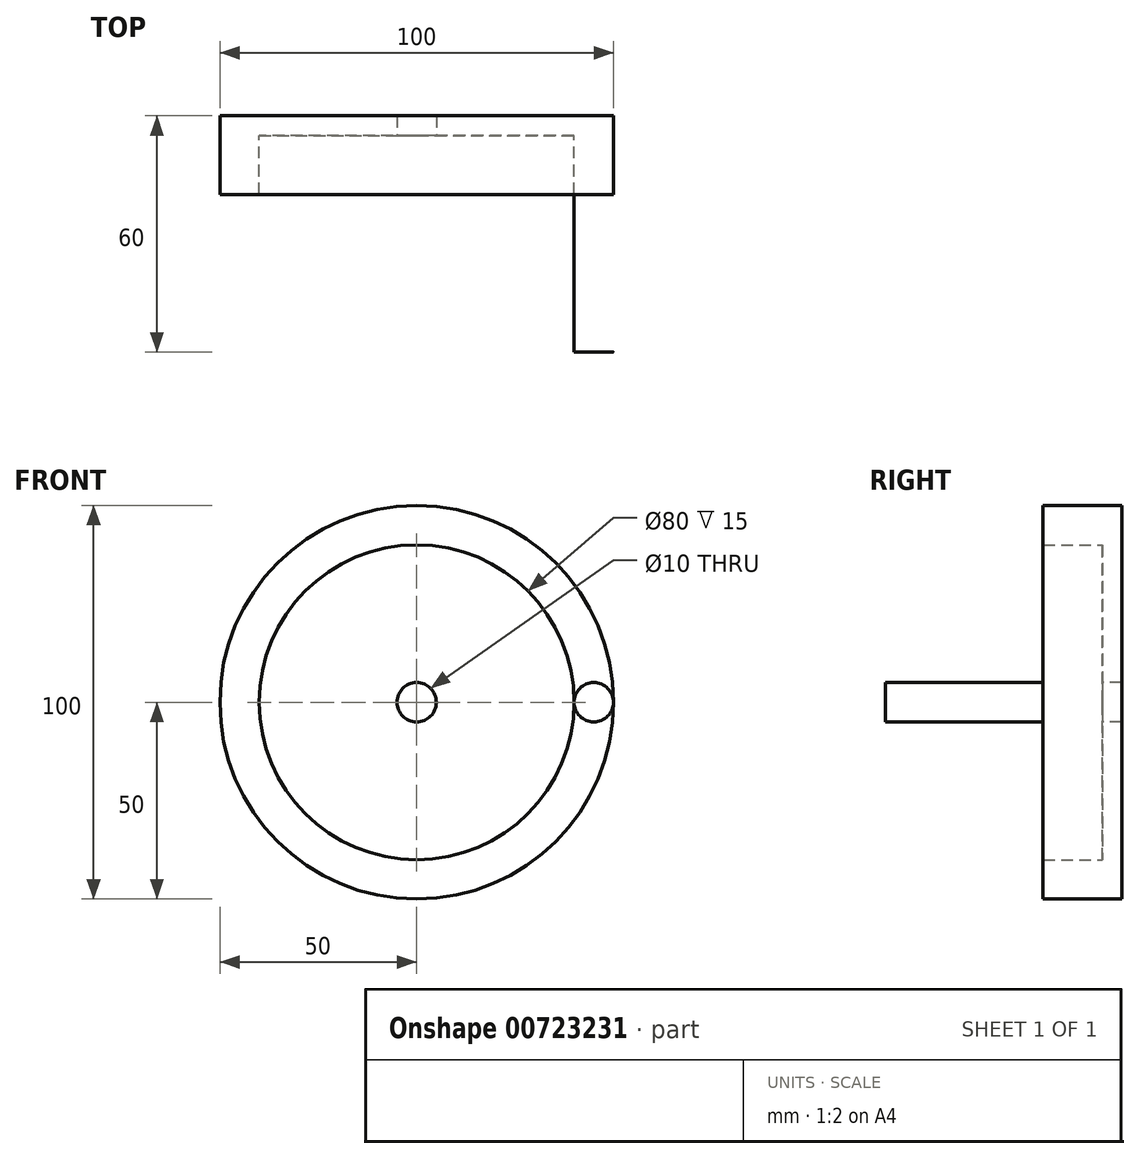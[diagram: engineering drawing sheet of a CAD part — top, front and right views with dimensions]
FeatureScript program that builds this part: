
annotation { "Feature Type Name" : "Feature", "Feature Type Description" : "" }
export const myFeature = defineFeature(function(context is Context, id is Id, definition is map)
    precondition{}
    {
        {
            var Q0;
            Q0=qCreatedBy(makeId("Front.planeOp"),FACE);
            var sketch = newSketch(context, id + "F0", { "sketchPlane" : qUnion([Q0])});
            skCircle(sketch, "E0", {"center": v(0, 0) * mm, "radius": 40 * mm});
            skCircle(sketch, "E1", {"center": v(0, 0) * mm, "radius": 50 * mm});
            skCircle(sketch, "E2", {"center": v(0, 0) * mm, "radius": 15 * mm});
            skCircle(sketch, "E3", {"center": v(0, 0) * mm, "radius": 5 * mm});
            skSolve(sketch);
        }
        {
            var Q0;
            Q0 = qSketchRegion(id + "F0", true);
            extrude(context, id + "F1", {"entities" : qUnion([Q0]), "depth" : 15 * mm, "offsetDistance" : 25 * mm});
        }
        {
            var Q0;
            Q0=makeQuery(id+"F1.opExtrude","CAP_FACE",FACE,{"disambiguationData":[OSD([sQuery(id+"F0.wireOp",EDGE,"E0"),sQuery(id+"F0.wireOp",EDGE,"E1")])],"isStart":true});
            var sketch = newSketch(context, id + "F2", { "sketchPlane" : qUnion([Q0])});
            skCircle(sketch, "E4", {"center": v(0, 0) * mm, "radius": 50 * mm});
            skCircle(sketch, "E5", {"center": v(0, 0) * mm, "radius": 5 * mm});
            skSolve(sketch);
        }
        {
            var Q0;
            Q0 = qSketchRegion(id + "F2", true);
            extrude(context, id + "F3", {"entities" : qUnion([Q0]), "operationType" : NewBodyOperationType.ADD, "depth" : 5 * mm, "offsetDistance" : 25 * mm});
        }
        {
            var Q0;
            Q0=makeQuery(id+"F1.opExtrude","CAP_FACE",FACE,{"disambiguationData":[OSD([sQuery(id+"F0.wireOp",EDGE,"E0"),sQuery(id+"F0.wireOp",EDGE,"E1")])],"isStart":false});
            var sketch = newSketch(context, id + "F4", { "sketchPlane" : qUnion([Q0])});
            skCircle(sketch, "E6", {"center": v(45, 0) * mm, "radius": 5 * mm});
            skSolve(sketch);
        }
        {
            var Q0;
            Q0 = qSketchRegion(id + "F4", true);
            extrude(context, id + "F5", {"entities" : qUnion([Q0]), "operationType" : NewBodyOperationType.ADD, "depth" : 40 * mm, "offsetDistance" : 25 * mm});
        }
    });
